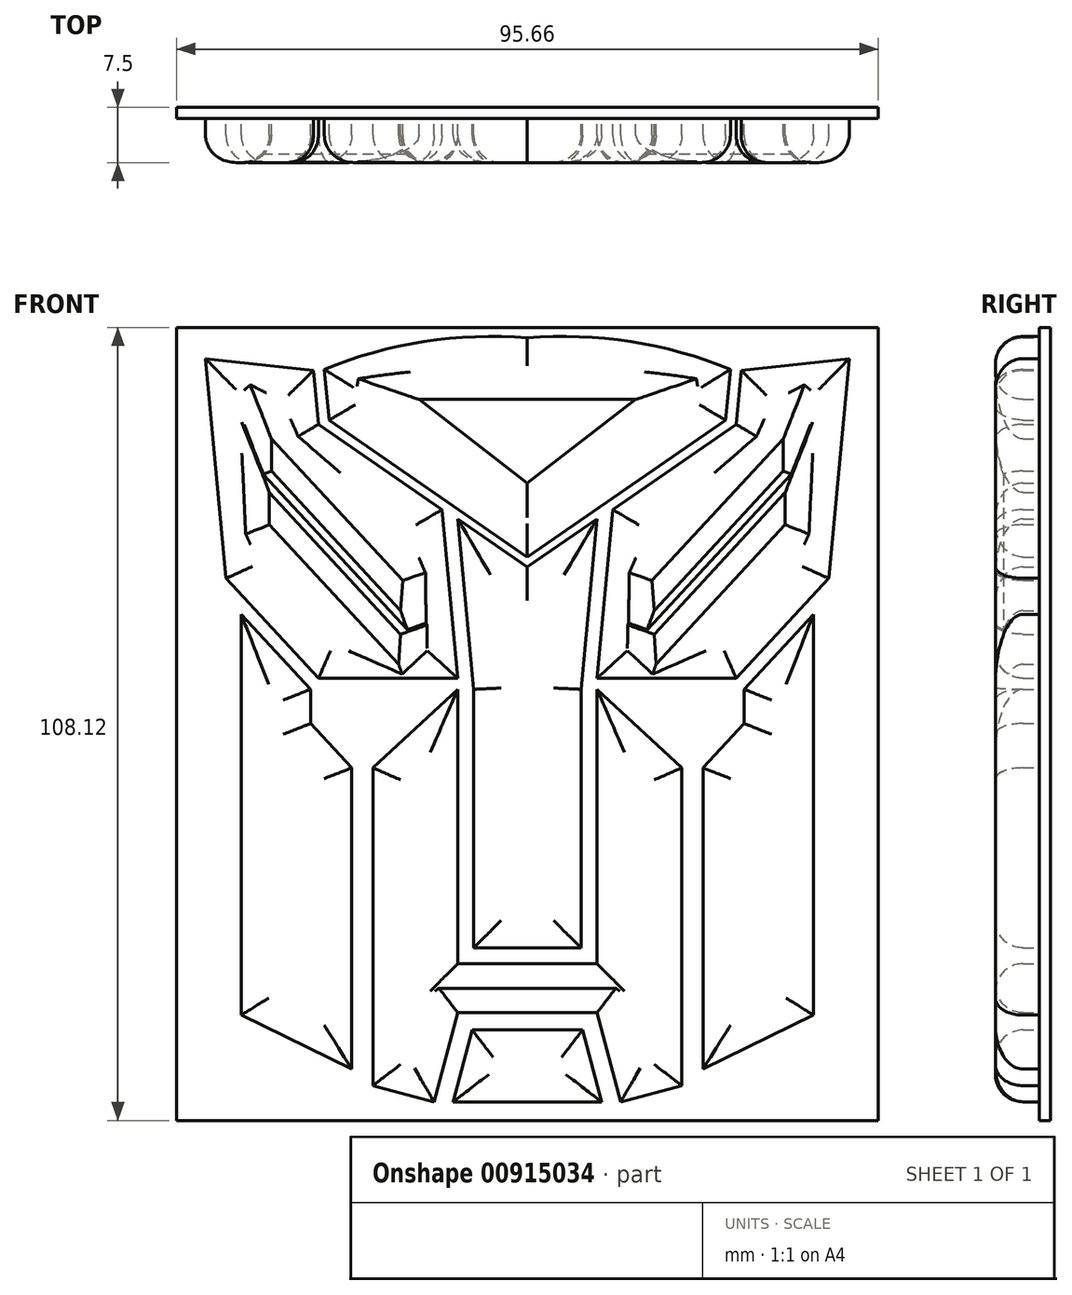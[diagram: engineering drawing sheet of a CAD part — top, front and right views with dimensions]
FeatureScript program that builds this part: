
annotation { "Feature Type Name" : "Feature", "Feature Type Description" : "" }
export const myFeature = defineFeature(function(context is Context, id is Id, definition is map)
    precondition{}
    {
        {
            var Q0;
            Q0=qCreatedBy(makeId("Front.planeOp"),FACE);
            var sketch = newSketch(context, id + "F0", { "sketchPlane" : qUnion([Q0])});
            skLineSegment(sketch, "E0", {"start": v(0, -75) * mm, "end": v(-13.5, -75) * mm});
            skLineSegment(sketch, "E1", {"start": v(-13.5, -75) * mm, "end": v(-10.03, -61.93) * mm});
            skLineSegment(sketch, "E2", {"start": v(-10.03, -61.93) * mm, "end": v(0, -61.93) * mm});
            skLineSegment(sketch, "E3", {"start": v(0, -61.93) * mm, "end": v(-10.03, -61.93) * mm});
            skLineSegment(sketch, "E4", {"start": v(-16.97, -75) * mm, "end": v(-12.67, -58.78) * mm});
            skLineSegment(sketch, "E5", {"start": v(-12.67, -58.78) * mm, "end": v(0, -58.78) * mm});
            skLineSegment(sketch, "E6", {"start": v(0, -58.78) * mm, "end": v(-12.67, -58.78) * mm});
            skLineSegment(sketch, "E7", {"start": v(-16.97, -75) * mm, "end": v(-28.09, -72.05) * mm});
            skLineSegment(sketch, "E8", {"start": v(-12.67, 0) * mm, "end": v(-12.67, -49.88) * mm});
            skLineSegment(sketch, "E9", {"start": v(-12.67, -49.88) * mm, "end": v(0, -49.88) * mm});
            skLineSegment(sketch, "E10", {"start": v(0, -49.88) * mm, "end": v(-12.67, -49.88) * mm});
            skLineSegment(sketch, "E11", {"start": v(-28.09, -72.05) * mm, "end": v(-28.09, -14.28) * mm});
            skLineSegment(sketch, "E12", {"start": v(-12.67, 0) * mm, "end": v(-28.09, -14.28) * mm});
            skLineSegment(sketch, "E13", {"start": v(-31.94, -69.04) * mm, "end": v(-31.94, -14.28) * mm});
            skLineSegment(sketch, "E14", {"start": v(-31.94, -14.28) * mm, "end": v(-39.4, -6.21) * mm});
            skLineSegment(sketch, "E15", {"start": v(-39.4, -6.21) * mm, "end": v(-39.4, 0) * mm});
            skLineSegment(sketch, "E16", {"start": v(-39.4, 0) * mm, "end": v(-52.05, 13.65) * mm});
            skLineSegment(sketch, "E17", {"start": v(-52.05, 13.65) * mm, "end": v(-52.05, -59.23) * mm});
            skLineSegment(sketch, "E18", {"start": v(-52.05, -59.23) * mm, "end": v(-31.94, -69.04) * mm});
            skLineSegment(sketch, "E19", {"start": v(0, -47.02) * mm, "end": v(-9.76, -47.02) * mm});
            skLineSegment(sketch, "E20", {"start": v(-9.76, -47.02) * mm, "end": v(-9.76, 0) * mm});
            skLineSegment(sketch, "E21", {"start": v(-9.76, 0) * mm, "end": v(-12.67, 30.98) * mm});
            skLineSegment(sketch, "E22", {"start": v(-12.67, 30.98) * mm, "end": v(0, 22.23) * mm});
            skLineSegment(sketch, "E23", {"start": v(0, 22.23) * mm, "end": v(-12.67, 30.98) * mm});
            skLineSegment(sketch, "E24", {"start": v(-37.98, 2.02) * mm, "end": v(-54.8, 20.19) * mm});
            skLineSegment(sketch, "E25", {"start": v(-54.8, 20.19) * mm, "end": v(-58.54, 60.12) * mm});
            skLineSegment(sketch, "E26", {"start": v(-58.54, 60.12) * mm, "end": v(-54.8, 20.19) * mm});
            skLineSegment(sketch, "E27", {"start": v(-37.98, 2.02) * mm, "end": v(-12.67, 2.02) * mm});
            skLineSegment(sketch, "E28", {"start": v(-12.67, 2.02) * mm, "end": v(-15.54, 32.66) * mm});
            skLineSegment(sketch, "E29", {"start": v(-15.54, 32.66) * mm, "end": v(-37.98, 48.16) * mm});
            skLineSegment(sketch, "E30", {"start": v(-37.98, 48.16) * mm, "end": v(-38.9, 57.97) * mm});
            skLineSegment(sketch, "E31", {"start": v(-38.9, 57.97) * mm, "end": v(-58.54, 60.12) * mm});
            skLineSegment(sketch, "E32", {"start": v(-36.92, 58.14) * mm, "end": v(-36.06, 48.94) * mm});
            skLineSegment(sketch, "E33", {"start": v(-36.06, 48.94) * mm, "end": v(0, 24.03) * mm});
            skLineSegment(sketch, "E34", {"start": v(0, 24.03) * mm, "end": v(-36.06, 48.94) * mm});
            skArc(sketch, "E35", {"start": v(0, 63.87) * mm, "mid": v(-18.8, 63.23) * mm, "end": v(-36.92, 58.14) * mm});
            skLineSegment(sketch, "E36", {"start": v(0, 52.7) * mm, "end": v(-19.72, 52.7) * mm});
            skLineSegment(sketch, "E37", {"start": v(-19.72, 52.7) * mm, "end": v(0, 37.5) * mm});
            skLineSegment(sketch, "E38.MirrorCS", {"start": v(12.67, -58.78) * mm, "end": v(0, -58.78) * mm});
            skLineSegment(sketch, "E39.MirrorCS", {"start": v(10.03, -61.93) * mm, "end": v(0, -61.93) * mm});
            skLineSegment(sketch, "E40.MirrorCS", {"start": v(58.54, 60.12) * mm, "end": v(54.8, 20.19) * mm});
            skLineSegment(sketch, "E41.MirrorCS", {"start": v(0, 24.03) * mm, "end": v(36.06, 48.94) * mm});
            skLineSegment(sketch, "E42.MirrorCS", {"start": v(12.67, -49.88) * mm, "end": v(0, -49.88) * mm});
            skLineSegment(sketch, "E43.MirrorCS", {"start": v(0, 22.23) * mm, "end": v(12.67, 30.98) * mm});
            skLineSegment(sketch, "E44.MirrorCS", {"start": v(0, -49.88) * mm, "end": v(12.67, -49.88) * mm});
            skLineSegment(sketch, "E45.MirrorCS", {"start": v(31.94, -14.28) * mm, "end": v(39.4, -6.21) * mm});
            skLineSegment(sketch, "E46.MirrorCS", {"start": v(36.92, 58.14) * mm, "end": v(36.06, 48.94) * mm});
            skArc(sketch, "E47.MirrorCS", {"start": v(0, 63.87) * mm, "mid": v(18.8, 63.23) * mm, "end": v(36.92, 58.14) * mm});
            skLineSegment(sketch, "E48.MirrorCS", {"start": v(54.8, 20.19) * mm, "end": v(58.54, 60.12) * mm});
            skLineSegment(sketch, "E49.MirrorCS", {"start": v(0, -58.78) * mm, "end": v(12.67, -58.78) * mm});
            skLineSegment(sketch, "E50.MirrorCS", {"start": v(0, -61.93) * mm, "end": v(10.03, -61.93) * mm});
            skLineSegment(sketch, "E51.MirrorCS", {"start": v(12.67, 0) * mm, "end": v(12.67, -49.88) * mm});
            skLineSegment(sketch, "E52.MirrorCS", {"start": v(31.94, -69.04) * mm, "end": v(31.94, -14.28) * mm});
            skLineSegment(sketch, "E53.MirrorCS", {"start": v(52.05, 13.65) * mm, "end": v(52.05, -59.23) * mm});
            skLineSegment(sketch, "E54.MirrorCS", {"start": v(9.76, 0) * mm, "end": v(12.67, 30.98) * mm});
            skLineSegment(sketch, "E55.MirrorCS", {"start": v(16.97, -75) * mm, "end": v(28.09, -72.05) * mm});
            skLineSegment(sketch, "E56.MirrorCS", {"start": v(15.54, 32.66) * mm, "end": v(37.98, 48.16) * mm});
            skLineSegment(sketch, "E57.MirrorCS", {"start": v(37.98, 2.02) * mm, "end": v(54.8, 20.19) * mm});
            skLineSegment(sketch, "E58.MirrorCS", {"start": v(28.09, -72.05) * mm, "end": v(28.09, -14.28) * mm});
            skLineSegment(sketch, "E59.MirrorCS", {"start": v(0, -47.02) * mm, "end": v(9.76, -47.02) * mm});
            skLineSegment(sketch, "E60.MirrorCS", {"start": v(19.72, 52.7) * mm, "end": v(0, 37.5) * mm});
            skLineSegment(sketch, "E61.MirrorCS", {"start": v(38.9, 57.97) * mm, "end": v(58.54, 60.12) * mm});
            skLineSegment(sketch, "E62.MirrorCS", {"start": v(13.5, -75) * mm, "end": v(10.03, -61.93) * mm});
            skLineSegment(sketch, "E63.MirrorCS", {"start": v(0, 52.7) * mm, "end": v(19.72, 52.7) * mm});
            skLineSegment(sketch, "E64.MirrorCS", {"start": v(39.4, -6.21) * mm, "end": v(39.4, 0) * mm});
            skLineSegment(sketch, "E65.MirrorCS", {"start": v(16.97, -75) * mm, "end": v(12.67, -58.78) * mm});
            skLineSegment(sketch, "E66.MirrorCS", {"start": v(0, -75) * mm, "end": v(13.5, -75) * mm});
            skLineSegment(sketch, "E67.MirrorCS", {"start": v(37.98, 48.16) * mm, "end": v(38.9, 57.97) * mm});
            skLineSegment(sketch, "E68.MirrorCS", {"start": v(12.67, 0) * mm, "end": v(28.09, -14.28) * mm});
            skLineSegment(sketch, "E69.MirrorCS", {"start": v(9.76, -47.02) * mm, "end": v(9.76, 0) * mm});
            skLineSegment(sketch, "E70.MirrorCS", {"start": v(52.05, -59.23) * mm, "end": v(31.94, -69.04) * mm});
            skLineSegment(sketch, "E71.MirrorCS", {"start": v(36.06, 48.94) * mm, "end": v(0, 24.03) * mm});
            skLineSegment(sketch, "E72.MirrorCS", {"start": v(37.98, 2.02) * mm, "end": v(12.67, 2.02) * mm});
            skLineSegment(sketch, "E73.MirrorCS", {"start": v(12.67, 30.98) * mm, "end": v(0, 22.23) * mm});
            skLineSegment(sketch, "E74.MirrorCS", {"start": v(39.4, 0) * mm, "end": v(52.05, 13.65) * mm});
            skLineSegment(sketch, "E75.MirrorCS", {"start": v(12.67, 2.02) * mm, "end": v(15.54, 32.66) * mm});
            skLineSegment(sketch, "E76", {"start": v(-23.04, 10.01) * mm, "end": v(-46.9, 35.78) * mm});
            skLineSegment(sketch, "E77", {"start": v(-46.9, 35.78) * mm, "end": v(-46.9, 29.92) * mm});
            skLineSegment(sketch, "E78", {"start": v(-46.9, 29.92) * mm, "end": v(-23.4, 4.54) * mm});
            skLineSegment(sketch, "E79", {"start": v(-23.4, 4.54) * mm, "end": v(-23.04, 10.01) * mm});
            skLineSegment(sketch, "E80", {"start": v(-22.68, 19.76) * mm, "end": v(-46.55, 45.53) * mm});
            skLineSegment(sketch, "E81", {"start": v(-46.55, 45.53) * mm, "end": v(-46.55, 39.67) * mm});
            skLineSegment(sketch, "E82", {"start": v(-46.55, 39.67) * mm, "end": v(-23.04, 14.29) * mm});
            skLineSegment(sketch, "E83", {"start": v(-23.04, 14.29) * mm, "end": v(-22.68, 19.76) * mm});
            skLineSegment(sketch, "E84.MirrorCS", {"start": v(22.68, 19.76) * mm, "end": v(46.55, 45.53) * mm});
            skLineSegment(sketch, "E85.MirrorCS", {"start": v(23.04, 10.01) * mm, "end": v(46.9, 35.78) * mm});
            skLineSegment(sketch, "E86.MirrorCS", {"start": v(46.55, 45.53) * mm, "end": v(46.55, 39.67) * mm});
            skLineSegment(sketch, "E87.MirrorCS", {"start": v(23.04, 14.29) * mm, "end": v(22.68, 19.76) * mm});
            skLineSegment(sketch, "E88.MirrorCS", {"start": v(46.55, 39.67) * mm, "end": v(23.04, 14.29) * mm});
            skLineSegment(sketch, "E89.MirrorCS", {"start": v(23.4, 4.54) * mm, "end": v(23.04, 10.01) * mm});
            skLineSegment(sketch, "E90.MirrorCS", {"start": v(46.9, 35.78) * mm, "end": v(46.9, 29.92) * mm});
            skLineSegment(sketch, "E91.MirrorCS", {"start": v(46.9, 29.92) * mm, "end": v(23.4, 4.54) * mm});
            skLineSegment(sketch, "E92", {"start": v(-9.76, 0) * mm, "end": v(-9.76, -47.02) * mm});
            skLineSegment(sketch, "E93", {"start": v(-9.76, 0) * mm, "end": v(9.76, 0) * mm});
            skLineSegment(sketch, "E94", {"start": v(9.76, 0) * mm, "end": v(9.76, -47.02) * mm});
            skLineSegment(sketch, "E95", {"start": v(9.76, -47.02) * mm, "end": v(-9.76, -47.02) * mm});
            skSolve(sketch);
        }
        {
            var Q0;
            Q0=qSketchRegion(id+"F0",true);
            var Q1;
            Q1=makeQuery(id+"F3MlLgJpoVEOoxf_0.opExtrude","CAP_FACE",FACE,{"disambiguationData":[OSD([sQuery(id+"F0.wireOp",EDGE,"E32"),sQuery(id+"F0.wireOp",EDGE,"E34"),sQuery(id+"F0.wireOp",EDGE,"E35"),sQuery(id+"F0.wireOp",EDGE,"E36"),sQuery(id+"F0.wireOp",EDGE,"E37"),sQuery(id+"F0.wireOp",EDGE,"E63.MirrorCS"),sQuery(id+"F0.wireOp",EDGE,"E71.MirrorCS"),sQuery(id+"F0.wireOp",EDGE,"E46.MirrorCS"),sQuery(id+"F0.wireOp",EDGE,"E60.MirrorCS"),sQuery(id+"F0.wireOp",EDGE,"E47.MirrorCS")])],"isStart":false});
            extrude(context, id + "F1", {"entities" : qUnion([Q0, Q1]), "depth" : 8 * mm, "offsetDistance" : 25 * mm});
        }
        {
            var Q0;
            Q0=makeQuery(id+"F3MlLgJpoVEOoxf_0.opExtrude","CAP_FACE",FACE,{"disambiguationData":[OSD([sQuery(id+"F0.wireOp",EDGE,"E45.MirrorCS"),sQuery(id+"F0.wireOp",EDGE,"E52.MirrorCS"),sQuery(id+"F0.wireOp",EDGE,"E64.MirrorCS"),sQuery(id+"F0.wireOp",EDGE,"E70.MirrorCS"),sQuery(id+"F0.wireOp",EDGE,"E53.MirrorCS"),sQuery(id+"F0.wireOp",EDGE,"E74.MirrorCS")])],"isStart":true});
            var Q1;
            Q1=makeQuery(id+"F3MlLgJpoVEOoxf_0.opExtrude","CAP_FACE",FACE,{"disambiguationData":[OSD([sQuery(id+"F0.wireOp",EDGE,"E48.MirrorCS"),sQuery(id+"F0.wireOp",EDGE,"E84.MirrorCS"),sQuery(id+"F0.wireOp",EDGE,"E85.MirrorCS"),sQuery(id+"F0.wireOp",EDGE,"E86.MirrorCS"),sQuery(id+"F0.wireOp",EDGE,"E87.MirrorCS"),sQuery(id+"F0.wireOp",EDGE,"E67.MirrorCS"),sQuery(id+"F0.wireOp",EDGE,"E61.MirrorCS"),sQuery(id+"F0.wireOp",EDGE,"E88.MirrorCS"),sQuery(id+"F0.wireOp",EDGE,"E75.MirrorCS"),sQuery(id+"F0.wireOp",EDGE,"E72.MirrorCS"),sQuery(id+"F0.wireOp",EDGE,"E89.MirrorCS"),sQuery(id+"F0.wireOp",EDGE,"E56.MirrorCS"),sQuery(id+"F0.wireOp",EDGE,"E90.MirrorCS"),sQuery(id+"F0.wireOp",EDGE,"E91.MirrorCS"),sQuery(id+"F0.wireOp",EDGE,"E57.MirrorCS")])],"isStart":true});
            var Q2;
            Q2=makeQuery(id+"F3MlLgJpoVEOoxf_0.opExtrude","CAP_FACE",FACE,{"disambiguationData":[OSD([sQuery(id+"F0.wireOp",EDGE,"E4"),sQuery(id+"F0.wireOp",EDGE,"E6"),sQuery(id+"F0.wireOp",EDGE,"E7"),sQuery(id+"F0.wireOp",EDGE,"E8"),sQuery(id+"F0.wireOp",EDGE,"E10"),sQuery(id+"F0.wireOp",EDGE,"E11"),sQuery(id+"F0.wireOp",EDGE,"E12"),sQuery(id+"F0.wireOp",EDGE,"E49.MirrorCS"),sQuery(id+"F0.wireOp",EDGE,"E68.MirrorCS"),sQuery(id+"F0.wireOp",EDGE,"E51.MirrorCS"),sQuery(id+"F0.wireOp",EDGE,"E55.MirrorCS"),sQuery(id+"F0.wireOp",EDGE,"E65.MirrorCS"),sQuery(id+"F0.wireOp",EDGE,"E58.MirrorCS"),sQuery(id+"F0.wireOp",EDGE,"E44.MirrorCS")])],"isStart":true});
            var Q3;
            Q3=makeQuery(id+"F3MlLgJpoVEOoxf_0.opExtrude","CAP_FACE",FACE,{"disambiguationData":[OSD([sQuery(id+"F0.wireOp",EDGE,"E24"),sQuery(id+"F0.wireOp",EDGE,"E26"),sQuery(id+"F0.wireOp",EDGE,"E27"),sQuery(id+"F0.wireOp",EDGE,"E28"),sQuery(id+"F0.wireOp",EDGE,"E29"),sQuery(id+"F0.wireOp",EDGE,"E30"),sQuery(id+"F0.wireOp",EDGE,"E31"),sQuery(id+"F0.wireOp",EDGE,"E76"),sQuery(id+"F0.wireOp",EDGE,"E77"),sQuery(id+"F0.wireOp",EDGE,"E78"),sQuery(id+"F0.wireOp",EDGE,"E79"),sQuery(id+"F0.wireOp",EDGE,"E80"),sQuery(id+"F0.wireOp",EDGE,"E81"),sQuery(id+"F0.wireOp",EDGE,"E82"),sQuery(id+"F0.wireOp",EDGE,"E83")])],"isStart":true});
            var Q4;
            Q4=makeQuery(id+"F3MlLgJpoVEOoxf_0.opExtrude","CAP_FACE",FACE,{"disambiguationData":[OSD([sQuery(id+"F0.wireOp",EDGE,"E13"),sQuery(id+"F0.wireOp",EDGE,"E14"),sQuery(id+"F0.wireOp",EDGE,"E15"),sQuery(id+"F0.wireOp",EDGE,"E16"),sQuery(id+"F0.wireOp",EDGE,"E17"),sQuery(id+"F0.wireOp",EDGE,"E18")])],"isStart":true});
            var Q5;
            Q5=makeQuery(id+"F3MlLgJpoVEOoxf_0.opExtrude","CAP_FACE",FACE,{"disambiguationData":[OSD([sQuery(id+"F0.wireOp",EDGE,"E0"),sQuery(id+"F0.wireOp",EDGE,"E1"),sQuery(id+"F0.wireOp",EDGE,"E3"),sQuery(id+"F0.wireOp",EDGE,"E66.MirrorCS"),sQuery(id+"F0.wireOp",EDGE,"E62.MirrorCS"),sQuery(id+"F0.wireOp",EDGE,"E50.MirrorCS")])],"isStart":true});
            var Q6;
            Q6=makeQuery(id+"F3MlLgJpoVEOoxf_0.opExtrude","CAP_FACE",FACE,{"disambiguationData":[OSD([sQuery(id+"F0.wireOp",EDGE,"E21"),sQuery(id+"F0.wireOp",EDGE,"E23"),sQuery(id+"F0.wireOp",EDGE,"E54.MirrorCS"),sQuery(id+"F0.wireOp",EDGE,"E73.MirrorCS"),sQuery(id+"F0.wireOp",EDGE,"E92"),sQuery(id+"F0.wireOp",EDGE,"E94"),sQuery(id+"F0.wireOp",EDGE,"E95")])],"isStart":true});
            var Q7;
            Q7=makeQuery(id+"F3MlLgJpoVEOoxf_0.opExtrude","CAP_FACE",FACE,{"disambiguationData":[OSD([sQuery(id+"F0.wireOp",EDGE,"E32"),sQuery(id+"F0.wireOp",EDGE,"E34"),sQuery(id+"F0.wireOp",EDGE,"E35"),sQuery(id+"F0.wireOp",EDGE,"E36"),sQuery(id+"F0.wireOp",EDGE,"E37"),sQuery(id+"F0.wireOp",EDGE,"E63.MirrorCS"),sQuery(id+"F0.wireOp",EDGE,"E71.MirrorCS"),sQuery(id+"F0.wireOp",EDGE,"E46.MirrorCS"),sQuery(id+"F0.wireOp",EDGE,"E60.MirrorCS"),sQuery(id+"F0.wireOp",EDGE,"E47.MirrorCS")])],"isStart":true});
            var Q8;
            Q8=makeQuery(id+"F1.opExtrude","CAP_FACE",FACE,{"disambiguationData":[OSD([sQuery(id+"F0.wireOp",EDGE,"E45.MirrorCS"),sQuery(id+"F0.wireOp",EDGE,"E52.MirrorCS"),sQuery(id+"F0.wireOp",EDGE,"E64.MirrorCS"),sQuery(id+"F0.wireOp",EDGE,"E70.MirrorCS"),sQuery(id+"F0.wireOp",EDGE,"E53.MirrorCS"),sQuery(id+"F0.wireOp",EDGE,"E74.MirrorCS")])],"isStart":false});
            var Q9;
            Q9=makeQuery(id+"F1.opExtrude","CAP_FACE",FACE,{"disambiguationData":[OSD([sQuery(id+"F0.wireOp",EDGE,"E4"),sQuery(id+"F0.wireOp",EDGE,"E6"),sQuery(id+"F0.wireOp",EDGE,"E7"),sQuery(id+"F0.wireOp",EDGE,"E8"),sQuery(id+"F0.wireOp",EDGE,"E10"),sQuery(id+"F0.wireOp",EDGE,"E11"),sQuery(id+"F0.wireOp",EDGE,"E12"),sQuery(id+"F0.wireOp",EDGE,"E49.MirrorCS"),sQuery(id+"F0.wireOp",EDGE,"E68.MirrorCS"),sQuery(id+"F0.wireOp",EDGE,"E51.MirrorCS"),sQuery(id+"F0.wireOp",EDGE,"E55.MirrorCS"),sQuery(id+"F0.wireOp",EDGE,"E65.MirrorCS"),sQuery(id+"F0.wireOp",EDGE,"E58.MirrorCS"),sQuery(id+"F0.wireOp",EDGE,"E44.MirrorCS")])],"isStart":false});
            var Q10;
            Q10=makeQuery(id+"F1.opExtrude","CAP_FACE",FACE,{"disambiguationData":[OSD([sQuery(id+"F0.wireOp",EDGE,"E0"),sQuery(id+"F0.wireOp",EDGE,"E1"),sQuery(id+"F0.wireOp",EDGE,"E3"),sQuery(id+"F0.wireOp",EDGE,"E66.MirrorCS"),sQuery(id+"F0.wireOp",EDGE,"E62.MirrorCS"),sQuery(id+"F0.wireOp",EDGE,"E50.MirrorCS")])],"isStart":false});
            var Q11;
            Q11=makeQuery(id+"F1.opExtrude","CAP_FACE",FACE,{"disambiguationData":[OSD([sQuery(id+"F0.wireOp",EDGE,"E21"),sQuery(id+"F0.wireOp",EDGE,"E23"),sQuery(id+"F0.wireOp",EDGE,"E54.MirrorCS"),sQuery(id+"F0.wireOp",EDGE,"E73.MirrorCS"),sQuery(id+"F0.wireOp",EDGE,"E92"),sQuery(id+"F0.wireOp",EDGE,"E94"),sQuery(id+"F0.wireOp",EDGE,"E95")])],"isStart":false});
            var Q12;
            {var subQ0=sQuery(id+"F0.wireOp",EDGE,"E47.MirrorCS");var subQ1=sQuery(id+"F0.wireOp",EDGE,"E60.MirrorCS");var subQ2=sQuery(id+"F0.wireOp",EDGE,"E46.MirrorCS");var subQ3=sQuery(id+"F0.wireOp",EDGE,"E71.MirrorCS");var subQ4=sQuery(id+"F0.wireOp",EDGE,"E63.MirrorCS");var subQ5=sQuery(id+"F0.wireOp",EDGE,"E37");var subQ6=sQuery(id+"F0.wireOp",EDGE,"E36");var subQ7=sQuery(id+"F0.wireOp",EDGE,"E35");var subQ8=sQuery(id+"F0.wireOp",EDGE,"E34");var subQ9=sQuery(id+"F0.wireOp",EDGE,"E32");Q12=makeQuery(id+"F1.opExtrude","CAP_FACE",FACE,{"disambiguationData":[OSD([subQ9,subQ8,subQ7,subQ6,subQ5,subQ4,subQ3,subQ2,subQ1,subQ0]),TDD([makeQuery(id+"F3MlLgJpoVEOoxf_0.opExtrude","CAP_FACE",FACE,{"disambiguationData":[OSD([subQ9,subQ8,subQ7,subQ6,subQ5,subQ4,subQ3,subQ2,subQ1,subQ0])],"isStart":false})])],"isStart":false});}
            var Q13;
            Q13=makeQuery(id+"F1.opExtrude","CAP_FACE",FACE,{"disambiguationData":[OSD([sQuery(id+"F0.wireOp",EDGE,"E24"),sQuery(id+"F0.wireOp",EDGE,"E26"),sQuery(id+"F0.wireOp",EDGE,"E27"),sQuery(id+"F0.wireOp",EDGE,"E28"),sQuery(id+"F0.wireOp",EDGE,"E29"),sQuery(id+"F0.wireOp",EDGE,"E30"),sQuery(id+"F0.wireOp",EDGE,"E31"),sQuery(id+"F0.wireOp",EDGE,"E76"),sQuery(id+"F0.wireOp",EDGE,"E77"),sQuery(id+"F0.wireOp",EDGE,"E78"),sQuery(id+"F0.wireOp",EDGE,"E79"),sQuery(id+"F0.wireOp",EDGE,"E80"),sQuery(id+"F0.wireOp",EDGE,"E81"),sQuery(id+"F0.wireOp",EDGE,"E82"),sQuery(id+"F0.wireOp",EDGE,"E83")])],"isStart":false});
            var Q14;
            Q14=makeQuery(id+"F1.opExtrude","CAP_FACE",FACE,{"disambiguationData":[OSD([sQuery(id+"F0.wireOp",EDGE,"E13"),sQuery(id+"F0.wireOp",EDGE,"E14"),sQuery(id+"F0.wireOp",EDGE,"E15"),sQuery(id+"F0.wireOp",EDGE,"E16"),sQuery(id+"F0.wireOp",EDGE,"E17"),sQuery(id+"F0.wireOp",EDGE,"E18")])],"isStart":false});
            var Q15;
            Q15=makeQuery(id+"F1.opExtrude","CAP_FACE",FACE,{"disambiguationData":[OSD([sQuery(id+"F0.wireOp",EDGE,"E48.MirrorCS"),sQuery(id+"F0.wireOp",EDGE,"E84.MirrorCS"),sQuery(id+"F0.wireOp",EDGE,"E85.MirrorCS"),sQuery(id+"F0.wireOp",EDGE,"E86.MirrorCS"),sQuery(id+"F0.wireOp",EDGE,"E87.MirrorCS"),sQuery(id+"F0.wireOp",EDGE,"E67.MirrorCS"),sQuery(id+"F0.wireOp",EDGE,"E61.MirrorCS"),sQuery(id+"F0.wireOp",EDGE,"E88.MirrorCS"),sQuery(id+"F0.wireOp",EDGE,"E75.MirrorCS"),sQuery(id+"F0.wireOp",EDGE,"E72.MirrorCS"),sQuery(id+"F0.wireOp",EDGE,"E89.MirrorCS"),sQuery(id+"F0.wireOp",EDGE,"E56.MirrorCS"),sQuery(id+"F0.wireOp",EDGE,"E90.MirrorCS"),sQuery(id+"F0.wireOp",EDGE,"E91.MirrorCS"),sQuery(id+"F0.wireOp",EDGE,"E57.MirrorCS")])],"isStart":false});
            fillet(context, id + "F2", {"entities" : qUnion([Q0, Q1, Q2, Q3, Q4, Q5, Q6, Q7, Q8, Q9, Q10, Q11, Q12, Q13, Q14, Q15]), "radius" : 5 * mm, "tangentPropagation" : true, "allowEdgeOverflow" : false});
        }
        {
            var Q0;
            Q0=qCreatedBy(makeId("Front.planeOp"),FACE);
            var sketch = newSketch(context, id + "F3", { "sketchPlane" : qUnion([Q0])});
            skLineSegment(sketch, "E96", {"start": v(0, 0) * mm, "end": v(63.77, 0) * mm});
            skLineSegment(sketch, "E97", {"start": v(63.77, 0) * mm, "end": v(63.77, 65.77) * mm});
            skLineSegment(sketch, "E98", {"start": v(63.77, 65.77) * mm, "end": v(0, 65.77) * mm});
            skLineSegment(sketch, "E99", {"start": v(0, 65.77) * mm, "end": v(0, 0) * mm});
            skLineSegment(sketch, "E100", {"start": v(63.77, 0) * mm, "end": v(63.77, -78.38) * mm});
            skLineSegment(sketch, "E101", {"start": v(63.77, -78.38) * mm, "end": v(0, -78.38) * mm});
            skLineSegment(sketch, "E102.MirrorCS", {"start": v(-63.77, 65.77) * mm, "end": v(0, 65.77) * mm});
            skLineSegment(sketch, "E103.MirrorCS", {"start": v(-63.77, 0) * mm, "end": v(-63.77, 65.77) * mm});
            skLineSegment(sketch, "E104.MirrorCS", {"start": v(-63.77, 0) * mm, "end": v(-63.77, -78.38) * mm});
            skLineSegment(sketch, "E105.MirrorCS", {"start": v(-63.77, -78.38) * mm, "end": v(0, -78.38) * mm});
            skSolve(sketch);
        }
        {
            var Q0;
            Q0=makeQuery(id+"F3.imprint","IMPRINT",FACE,{"disambiguationData":[TD([[makeQuery(id+"F3.imprint","IMPRINT",EDGE,{"derivedFrom":sQuery(id+"F3.wireOp",EDGE,"E96")}),-1.0]])]});
            var Q1;
            Q1=makeQuery(id+"F3.imprint","IMPRINT",FACE,{"disambiguationData":[TD([[makeQuery(id+"F3.imprint","IMPRINT",EDGE,{"derivedFrom":sQuery(id+"F3.wireOp",EDGE,"E96")}),1.0]])]});
            extrude(context, id + "F4", {"entities" : qUnion([Q0, Q1]), "oppositeDirection" : true, "depth" : 2 * mm, "offsetDistance" : 25 * mm});
        }
        {
            var Q0;
            Q0=makeQuery(id+"F4.opExtrude","SWEPT_BODY",BODY,{"disambiguationData":[OSD([sQuery(id+"F3.wireOp",EDGE,"E97"),sQuery(id+"F3.wireOp",EDGE,"E98"),sQuery(id+"F3.wireOp",EDGE,"E100"),sQuery(id+"F3.wireOp",EDGE,"E101"),sQuery(id+"F3.wireOp",EDGE,"E102.MirrorCS"),sQuery(id+"F3.wireOp",EDGE,"E103.MirrorCS"),sQuery(id+"F3.wireOp",EDGE,"E104.MirrorCS"),sQuery(id+"F3.wireOp",EDGE,"E105.MirrorCS")])]});
            var Q1;
            Q1=makeQuery(id+"F1.opExtrude","SWEPT_BODY",BODY,{"disambiguationData":[OSD([sQuery(id+"F0.wireOp",EDGE,"E0"),sQuery(id+"F0.wireOp",EDGE,"E1"),sQuery(id+"F0.wireOp",EDGE,"E3"),sQuery(id+"F0.wireOp",EDGE,"E66.MirrorCS"),sQuery(id+"F0.wireOp",EDGE,"E62.MirrorCS"),sQuery(id+"F0.wireOp",EDGE,"E50.MirrorCS")])]});
            var Q2;
            Q2=makeQuery(id+"F1.opExtrude","SWEPT_BODY",BODY,{"disambiguationData":[OSD([sQuery(id+"F0.wireOp",EDGE,"E21"),sQuery(id+"F0.wireOp",EDGE,"E23"),sQuery(id+"F0.wireOp",EDGE,"E54.MirrorCS"),sQuery(id+"F0.wireOp",EDGE,"E73.MirrorCS"),sQuery(id+"F0.wireOp",EDGE,"E92"),sQuery(id+"F0.wireOp",EDGE,"E94"),sQuery(id+"F0.wireOp",EDGE,"E95")])]});
            var Q3;
            Q3=makeQuery(id+"F1.opExtrude","SWEPT_BODY",BODY,{"disambiguationData":[OSD([sQuery(id+"F0.wireOp",EDGE,"E13"),sQuery(id+"F0.wireOp",EDGE,"E14"),sQuery(id+"F0.wireOp",EDGE,"E15"),sQuery(id+"F0.wireOp",EDGE,"E16"),sQuery(id+"F0.wireOp",EDGE,"E17"),sQuery(id+"F0.wireOp",EDGE,"E18")])]});
            var Q4;
            Q4=makeQuery(id+"F1.opExtrude","SWEPT_BODY",BODY,{"disambiguationData":[OSD([sQuery(id+"F0.wireOp",EDGE,"E4"),sQuery(id+"F0.wireOp",EDGE,"E6"),sQuery(id+"F0.wireOp",EDGE,"E7"),sQuery(id+"F0.wireOp",EDGE,"E8"),sQuery(id+"F0.wireOp",EDGE,"E10"),sQuery(id+"F0.wireOp",EDGE,"E11"),sQuery(id+"F0.wireOp",EDGE,"E12"),sQuery(id+"F0.wireOp",EDGE,"E49.MirrorCS"),sQuery(id+"F0.wireOp",EDGE,"E68.MirrorCS"),sQuery(id+"F0.wireOp",EDGE,"E51.MirrorCS"),sQuery(id+"F0.wireOp",EDGE,"E55.MirrorCS"),sQuery(id+"F0.wireOp",EDGE,"E65.MirrorCS"),sQuery(id+"F0.wireOp",EDGE,"E58.MirrorCS"),sQuery(id+"F0.wireOp",EDGE,"E44.MirrorCS")])]});
            var Q5;
            Q5=makeQuery(id+"F1.opExtrude","SWEPT_BODY",BODY,{"disambiguationData":[OSD([sQuery(id+"F0.wireOp",EDGE,"E45.MirrorCS"),sQuery(id+"F0.wireOp",EDGE,"E52.MirrorCS"),sQuery(id+"F0.wireOp",EDGE,"E64.MirrorCS"),sQuery(id+"F0.wireOp",EDGE,"E70.MirrorCS"),sQuery(id+"F0.wireOp",EDGE,"E53.MirrorCS"),sQuery(id+"F0.wireOp",EDGE,"E74.MirrorCS")])]});
            var Q6;
            Q6=makeQuery(id+"F1.opExtrude","SWEPT_BODY",BODY,{"disambiguationData":[OSD([sQuery(id+"F0.wireOp",EDGE,"E32"),sQuery(id+"F0.wireOp",EDGE,"E34"),sQuery(id+"F0.wireOp",EDGE,"E35"),sQuery(id+"F0.wireOp",EDGE,"E36"),sQuery(id+"F0.wireOp",EDGE,"E37"),sQuery(id+"F0.wireOp",EDGE,"E63.MirrorCS"),sQuery(id+"F0.wireOp",EDGE,"E71.MirrorCS"),sQuery(id+"F0.wireOp",EDGE,"E46.MirrorCS"),sQuery(id+"F0.wireOp",EDGE,"E60.MirrorCS"),sQuery(id+"F0.wireOp",EDGE,"E47.MirrorCS")])]});
            var Q7;
            Q7=makeQuery(id+"F1.opExtrude","SWEPT_BODY",BODY,{"disambiguationData":[OSD([sQuery(id+"F0.wireOp",EDGE,"E24"),sQuery(id+"F0.wireOp",EDGE,"E26"),sQuery(id+"F0.wireOp",EDGE,"E27"),sQuery(id+"F0.wireOp",EDGE,"E28"),sQuery(id+"F0.wireOp",EDGE,"E29"),sQuery(id+"F0.wireOp",EDGE,"E30"),sQuery(id+"F0.wireOp",EDGE,"E31"),sQuery(id+"F0.wireOp",EDGE,"E76"),sQuery(id+"F0.wireOp",EDGE,"E77"),sQuery(id+"F0.wireOp",EDGE,"E78"),sQuery(id+"F0.wireOp",EDGE,"E79"),sQuery(id+"F0.wireOp",EDGE,"E80"),sQuery(id+"F0.wireOp",EDGE,"E81"),sQuery(id+"F0.wireOp",EDGE,"E82"),sQuery(id+"F0.wireOp",EDGE,"E83")])]});
            var Q8;
            Q8=makeQuery(id+"F1.opExtrude","SWEPT_BODY",BODY,{"disambiguationData":[OSD([sQuery(id+"F0.wireOp",EDGE,"E48.MirrorCS"),sQuery(id+"F0.wireOp",EDGE,"E84.MirrorCS"),sQuery(id+"F0.wireOp",EDGE,"E85.MirrorCS"),sQuery(id+"F0.wireOp",EDGE,"E86.MirrorCS"),sQuery(id+"F0.wireOp",EDGE,"E87.MirrorCS"),sQuery(id+"F0.wireOp",EDGE,"E67.MirrorCS"),sQuery(id+"F0.wireOp",EDGE,"E61.MirrorCS"),sQuery(id+"F0.wireOp",EDGE,"E88.MirrorCS"),sQuery(id+"F0.wireOp",EDGE,"E75.MirrorCS"),sQuery(id+"F0.wireOp",EDGE,"E72.MirrorCS"),sQuery(id+"F0.wireOp",EDGE,"E89.MirrorCS"),sQuery(id+"F0.wireOp",EDGE,"E56.MirrorCS"),sQuery(id+"F0.wireOp",EDGE,"E90.MirrorCS"),sQuery(id+"F0.wireOp",EDGE,"E91.MirrorCS"),sQuery(id+"F0.wireOp",EDGE,"E57.MirrorCS")])]});
            var Q9;
            Q9=qCreatedBy(makeId("Origin.pointOp"),VERTEX);
            transform(context, id + "F5", {"entities" : qUnion([Q0, Q1, Q2, Q3, Q4, Q5, Q6, Q7, Q8]), "transformType" : TransformType.SCALE_UNIFORMLY, "scale" : .75, "scalePoint" : qUnion([Q9]), "makeCopy" : false});
        }
    });
